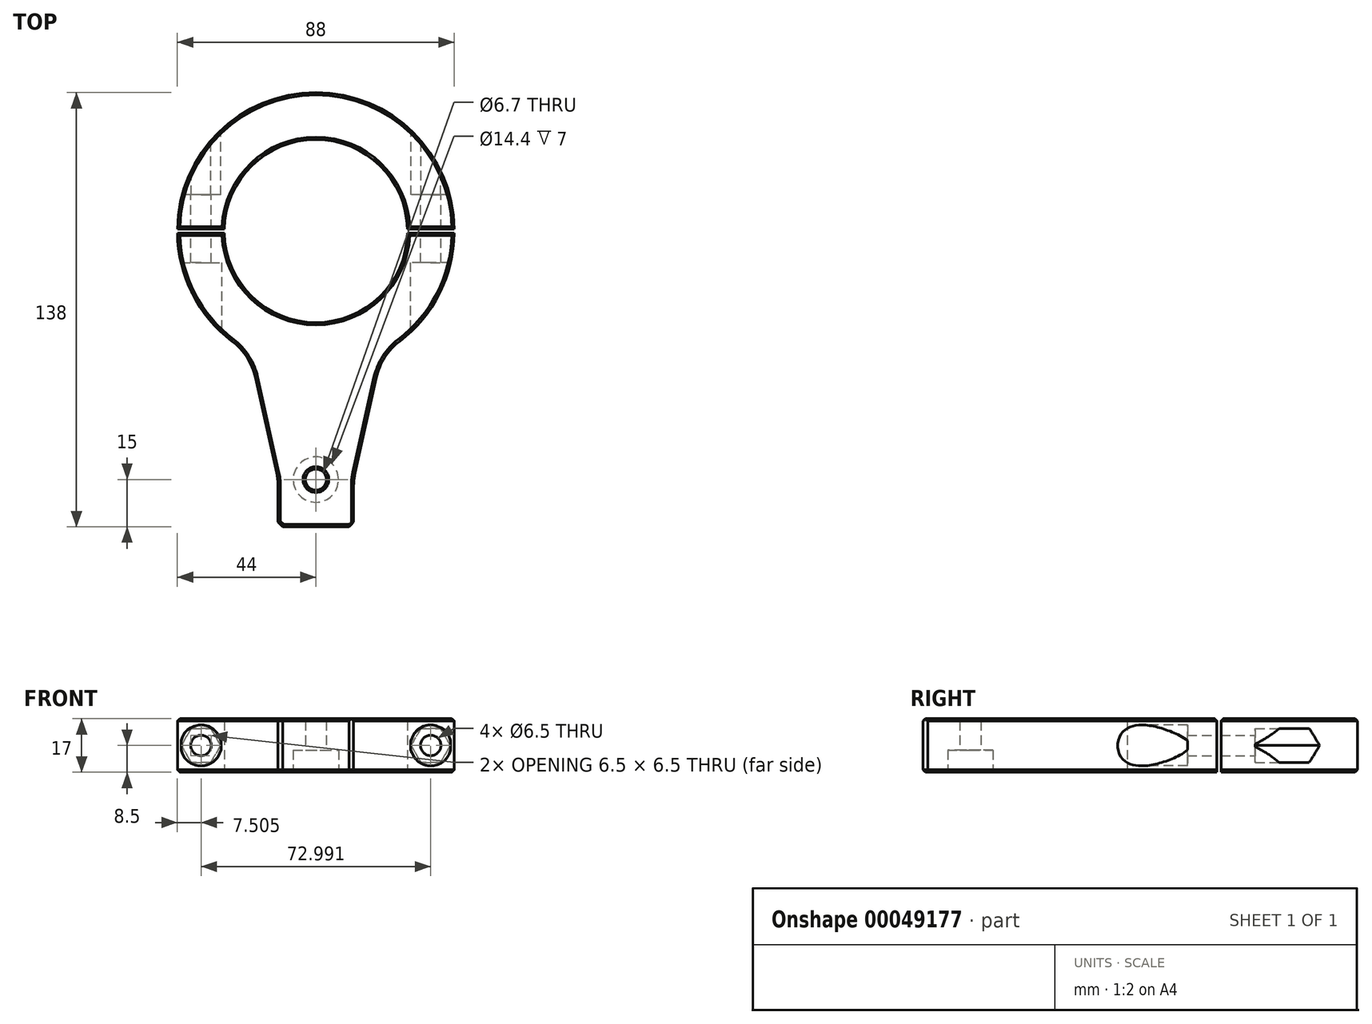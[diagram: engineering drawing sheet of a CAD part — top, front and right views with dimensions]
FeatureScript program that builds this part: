
annotation { "Feature Type Name" : "Feature", "Feature Type Description" : "" }
export const myFeature = defineFeature(function(context is Context, id is Id, definition is map)
    precondition{}
    {
        {
            var Q0;
            Q0=qCreatedBy(makeId("Top.planeOp"),FACE);
            var sketch = newSketch(context, id + "F0", { "sketchPlane" : qUnion([Q0])});
            skArc(sketch, "E0", {"start": v(-29.1, -0.64) * mm, "mid": v(0, -29.1) * mm, "end": v(29.1, -0.64) * mm});
            skArc(sketch, "E1", {"start": v(20.98, -38.68) * mm, "mid": v(37.64, -22.78) * mm, "end": v(44, -0.64) * mm});
            skLineSegment(sketch, "E2.top", {"start": v(-12, -94) * mm, "end": v(12, -94) * mm});
            skLineSegment(sketch, "E2.left", {"start": v(-12, -79) * mm, "end": v(-12, -94) * mm});
            skLineSegment(sketch, "E2.right", {"start": v(12, -79) * mm, "end": v(12, -94) * mm});
            skCircle(sketch, "E3", {"center": v(0, -79) * mm, "radius": 3.35 * mm});
            skPoint(sketch, "E3.centerSnap0", {"position": v(0, -94) * mm});
            skLineSegment(sketch, "E4", {"start": v(-12, -79) * mm, "end": v(-20.98, -38.68) * mm});
            skLineSegment(sketch, "E5", {"start": v(20.98, -38.68) * mm, "end": v(12, -79) * mm});
            skPoint(sketch, "E6.orphan", {"position": v(-12, 0) * mm});
            skLineSegment(sketch, "E7.bottom", {"start": v(-44, 0.64) * mm, "end": v(-29.1, 0.64) * mm});
            skLineSegment(sketch, "E7.top", {"start": v(-44, -0.64) * mm, "end": v(-29.1, -0.64) * mm});
            skLineSegment(sketch, "E8.trimOffspring", {"start": v(29.1, -0.64) * mm, "end": v(44, -0.64) * mm});
            skLineSegment(sketch, "E9.trimOffspring", {"start": v(29.1, 0.64) * mm, "end": v(44, 0.64) * mm});
            skArc(sketch, "E10.trimOffspring", {"start": v(-44, -0.64) * mm, "mid": v(-37.64, -22.78) * mm, "end": v(-20.98, -38.68) * mm});
            skArc(sketch, "E11.trimOffspring", {"start": v(29.1, 0.64) * mm, "mid": v(0, 29.1) * mm, "end": v(-29.1, 0.64) * mm});
            skArc(sketch, "E12.trimOffspring", {"start": v(44, 0.64) * mm, "mid": v(0, 44) * mm, "end": v(-44, 0.64) * mm});
            skSolve(sketch);
        }
        {
            var Q0;
            Q0 = qSketchRegion(id + "F0", true);
            extrude(context, id + "F1", {"entities" : qUnion([Q0]), "depth" : 17 * mm});
        }
        {
            var Q0;
            Q0=makeQuery(id+"F1.opExtrude","CAP_FACE",FACE,{"disambiguationData":[OSD([sQuery(id+"F0.wireOp",EDGE,"E0"),sQuery(id+"F0.wireOp",EDGE,"E1"),sQuery(id+"F0.wireOp",EDGE,"E2.top"),sQuery(id+"F0.wireOp",EDGE,"E2.left"),sQuery(id+"F0.wireOp",EDGE,"E2.right"),sQuery(id+"F0.wireOp",EDGE,"E3"),sQuery(id+"F0.wireOp",EDGE,"E4"),sQuery(id+"F0.wireOp",EDGE,"E5")])],"isStart":true});
            var sketch = newSketch(context, id + "F2", { "sketchPlane" : qUnion([Q0])});
            skCircle(sketch, "E13", {"center": v(0, 79) * mm, "radius": 7.2 * mm});
            skSolve(sketch);
        }
        {
            var Q0;
            Q0 = qSketchRegion(id + "F2", true);
            extrude(context, id + "F3", {"entities" : qUnion([Q0]), "operationType" : NewBodyOperationType.REMOVE, "oppositeDirection" : true, "depth" : 7 * mm});
        }
        {
            var Q0;
            Q0=makeQuery(id+"F1.opExtrude","SWEPT_EDGE",EDGE,{"disambiguationData":[OSD([sQuery(id+"F0.wireOp",EDGE,"E4"),sQuery(id+"F0.wireOp",EDGE,"E10.trimOffspring")])]});
            var Q1;
            Q1=makeQuery(id+"F1.opExtrude","SWEPT_EDGE",EDGE,{"disambiguationData":[OSD([sQuery(id+"F0.wireOp",EDGE,"E2.left"),sQuery(id+"F0.wireOp",EDGE,"E4")])]});
            var Q2;
            Q2=makeQuery(id+"F1.opExtrude","SWEPT_EDGE",EDGE,{"disambiguationData":[OSD([sQuery(id+"F0.wireOp",EDGE,"E1"),sQuery(id+"F0.wireOp",EDGE,"E5")])]});
            var Q3;
            Q3=makeQuery(id+"F1.opExtrude","SWEPT_EDGE",EDGE,{"disambiguationData":[OSD([sQuery(id+"F0.wireOp",EDGE,"E2.right"),sQuery(id+"F0.wireOp",EDGE,"E5")])]});
            fillet(context, id + "F4", {"entities" : qUnion([Q0, Q1, Q2, Q3]), "radius" : 20 * mm, "tangentPropagation" : true, "allowEdgeOverflow" : false});
        }
        {
            var Q0;
            Q0=qCreatedBy(makeId("Front.planeOp"),FACE);
            cPlane(context, id + "F5", {"entities" : qUnion([Q0]), "cplaneType" : CPlaneType.OFFSET, "offset" : 50 * mm, "oppositeDirection" : true, "width" : 150 * mm, "height" : 150 * mm});
        }
        {
            var Q0;
            Q0=qCreatedBy(id+"F5.planeOp",FACE);
            var sketch = newSketch(context, id + "F6", { "sketchPlane" : qUnion([Q0])});
            skCircle(sketch, "E14", {"center": v(36.5, 8.5) * mm, "radius": 3.25 * mm});
            skCircle(sketch, "E15", {"center": v(-36.5, 8.5) * mm, "radius": 3.25 * mm});
            skSolve(sketch);
        }
        {
            var Q0;
            Q0 = qSketchRegion(id + "F6", true);
            extrude(context, id + "F7", {"entities" : qUnion([Q0]), "operationType" : NewBodyOperationType.REMOVE, "depth" : 100 * mm});
        }
        {
            var Q0;
            Q0=qCreatedBy(id+"F5.planeOp",FACE);
            var sketch = newSketch(context, id + "F8", { "sketchPlane" : qUnion([Q0])});
            skCircle(sketch, "E16.cCircle", {"center": v(36.5, 8.5) * mm, "radius": 5.4 * mm, "construction": true});
            skLineSegment(sketch, "E16.0", {"start": v(33.38, 3.1) * mm, "end": v(30.26, 8.5) * mm});
            skLineSegment(sketch, "E16.1", {"start": v(30.26, 8.5) * mm, "end": v(33.38, 13.9) * mm});
            skLineSegment(sketch, "E16.2", {"start": v(33.38, 13.9) * mm, "end": v(39.61, 13.9) * mm});
            skLineSegment(sketch, "E16.3", {"start": v(39.61, 13.9) * mm, "end": v(42.73, 8.5) * mm});
            skLineSegment(sketch, "E16.4", {"start": v(42.73, 8.5) * mm, "end": v(39.61, 3.1) * mm});
            skLineSegment(sketch, "E16.5", {"start": v(39.61, 3.1) * mm, "end": v(33.38, 3.1) * mm});
            skPoint(sketch, "E16.0.midPoint", {"position": v(31.82, 5.8) * mm});
            skCircle(sketch, "E17.cCircle", {"center": v(-36.5, 8.5) * mm, "radius": 5.4 * mm, "construction": true});
            skLineSegment(sketch, "E17.0", {"start": v(-39.61, 3.1) * mm, "end": v(-42.73, 8.5) * mm});
            skLineSegment(sketch, "E17.1", {"start": v(-42.73, 8.5) * mm, "end": v(-39.61, 13.9) * mm});
            skLineSegment(sketch, "E17.2", {"start": v(-39.61, 13.9) * mm, "end": v(-33.38, 13.9) * mm});
            skLineSegment(sketch, "E17.3", {"start": v(-33.38, 13.9) * mm, "end": v(-30.26, 8.5) * mm});
            skLineSegment(sketch, "E17.4", {"start": v(-30.26, 8.5) * mm, "end": v(-33.38, 3.1) * mm});
            skLineSegment(sketch, "E17.5", {"start": v(-33.38, 3.1) * mm, "end": v(-39.61, 3.1) * mm});
            skPoint(sketch, "E17.0.midPoint", {"position": v(-41.17, 5.8) * mm});
            skSolve(sketch);
        }
        {
            var Q0;
            Q0 = qSketchRegion(id + "F8", true);
            extrude(context, id + "F9", {"entities" : qUnion([Q0]), "operationType" : NewBodyOperationType.REMOVE, "depth" : 38.5 * mm});
        }
        {
            var Q0;
            Q0=qCreatedBy(makeId("Front.planeOp"),FACE);
            cPlane(context, id + "F10", {"entities" : qUnion([Q0]), "cplaneType" : CPlaneType.OFFSET, "offset" : 40 * mm, "width" : 150 * mm, "height" : 150 * mm});
        }
        {
            var Q0;
            Q0=qCreatedBy(id+"F10.planeOp",FACE);
            var sketch = newSketch(context, id + "F11", { "sketchPlane" : qUnion([Q0])});
            skCircle(sketch, "E18", {"center": v(-36.5, 8.5) * mm, "radius": 6.5 * mm});
            skCircle(sketch, "E19", {"center": v(36.5, 8.5) * mm, "radius": 6.5 * mm});
            skSolve(sketch);
        }
        {
            var Q0;
            Q0=makeQuery(id+"F11.imprint","IMPRINT",FACE,{"disambiguationData":[TD([[makeQuery(id+"F11.imprint","IMPRINT",EDGE,{"derivedFrom":sQuery(id+"F11.wireOp",EDGE,"E18")}),1.0]])]});
            var Q1;
            Q1=makeQuery(id+"F11.imprint","IMPRINT",FACE,{"disambiguationData":[TD([[makeQuery(id+"F11.imprint","IMPRINT",EDGE,{"derivedFrom":sQuery(id+"F11.wireOp",EDGE,"E19")}),1.0]])]});
            extrude(context, id + "F12", {"entities" : qUnion([Q0, Q1]), "operationType" : NewBodyOperationType.REMOVE, "oppositeDirection" : true, "depth" : 30 * mm});
        }
        {
            var Q0;
            Q0=makeQuery(id+"F1.opExtrude","SWEPT_EDGE",EDGE,{"disambiguationData":[OSD([sQuery(id+"F0.wireOp",EDGE,"E2.top"),sQuery(id+"F0.wireOp",EDGE,"E2.left")])]});
            var Q1;
            Q1=makeQuery(id+"F1.opExtrude","SWEPT_EDGE",EDGE,{"disambiguationData":[OSD([sQuery(id+"F0.wireOp",EDGE,"E2.top"),sQuery(id+"F0.wireOp",EDGE,"E2.right")])]});
            chamfer(context, id + "F13", {"entities" : qUnion([Q0, Q1]), "width" : 1.5 * mm, "tangentPropagation" : true});
        }
        {
            var Q0;
            Q0=makeQuery(id+"F1.opExtrude","CAP_EDGE",EDGE,{"disambiguationData":[OSD([sQuery(id+"F0.wireOp",EDGE,"E3")])],"isStart":false});
            var Q1;
            Q1=makeQuery(id+"F1.opExtrude","CAP_EDGE",EDGE,{"disambiguationData":[OSD([sQuery(id+"F0.wireOp",EDGE,"E0")])],"isStart":false});
            var Q2;
            Q2=makeQuery(id+"F1.opExtrude","CAP_EDGE",EDGE,{"disambiguationData":[OSD([sQuery(id+"F0.wireOp",EDGE,"E11.trimOffspring")])],"isStart":false});
            var Q3;
            Q3=makeQuery(id+"F1.opExtrude","CAP_EDGE",EDGE,{"disambiguationData":[OSD([sQuery(id+"F0.wireOp",EDGE,"E9.trimOffspring")])],"isStart":false});
            var Q4;
            Q4=makeQuery(id+"F1.opExtrude","CAP_EDGE",EDGE,{"disambiguationData":[OSD([sQuery(id+"F0.wireOp",EDGE,"E8.trimOffspring")])],"isStart":false});
            var Q5;
            Q5=makeQuery(id+"F1.opExtrude","CAP_EDGE",EDGE,{"disambiguationData":[OSD([sQuery(id+"F0.wireOp",EDGE,"E7.bottom")])],"isStart":false});
            var Q6;
            Q6=makeQuery(id+"F1.opExtrude","CAP_EDGE",EDGE,{"disambiguationData":[OSD([sQuery(id+"F0.wireOp",EDGE,"E7.top")])],"isStart":false});
            var Q7;
            Q7=makeQuery(id+"F3.boolean.opBoolean","COPY",EDGE,{"derivedFrom":makeQuery(id+"F3.opExtrude","CAP_EDGE",EDGE,{"disambiguationData":[OSD([sQuery(id+"F2.wireOp",EDGE,"E13")])],"isStart":true})});
            var Q8;
            Q8=makeQuery(id+"F1.opExtrude","CAP_EDGE",EDGE,{"disambiguationData":[OSD([sQuery(id+"F0.wireOp",EDGE,"E0")])],"isStart":true});
            var Q9;
            Q9=makeQuery(id+"F1.opExtrude","CAP_EDGE",EDGE,{"disambiguationData":[OSD([sQuery(id+"F0.wireOp",EDGE,"E11.trimOffspring")])],"isStart":true});
            var Q10;
            Q10=makeQuery(id+"F1.opExtrude","CAP_EDGE",EDGE,{"disambiguationData":[OSD([sQuery(id+"F0.wireOp",EDGE,"E1")])],"isStart":true});
            var Q11;
            {var subQ0=sQuery(id+"F0.wireOp",EDGE,"E1");var subQ1=sQuery(id+"F0.wireOp",EDGE,"E5");Q11=makeQuery(id+"F4.opFillet","BLEND_EDGE",EDGE,{"blendedFrom":[makeQuery(id+"F1.opExtrude","SWEPT_EDGE",EDGE,{"disambiguationData":[OSD([subQ0,subQ1])]}),makeQuery(id+"F1.opExtrude","CAP_FACE",FACE,{"disambiguationData":[OSD([sQuery(id+"F0.wireOp",EDGE,"E0"),subQ0,sQuery(id+"F0.wireOp",EDGE,"E2.top"),sQuery(id+"F0.wireOp",EDGE,"E2.left"),sQuery(id+"F0.wireOp",EDGE,"E2.right"),sQuery(id+"F0.wireOp",EDGE,"E3"),sQuery(id+"F0.wireOp",EDGE,"E4"),subQ1,sQuery(id+"F0.wireOp",EDGE,"E7.top"),sQuery(id+"F0.wireOp",EDGE,"E8.trimOffspring"),sQuery(id+"F0.wireOp",EDGE,"E10.trimOffspring")])],"isStart":true})],"blendedInto":[makeQuery(id+"F1.opExtrude","CAP_FACE",FACE,{"disambiguationData":[OSD([sQuery(id+"F0.wireOp",EDGE,"E0"),subQ0,sQuery(id+"F0.wireOp",EDGE,"E2.top"),sQuery(id+"F0.wireOp",EDGE,"E2.left"),sQuery(id+"F0.wireOp",EDGE,"E2.right"),sQuery(id+"F0.wireOp",EDGE,"E3"),sQuery(id+"F0.wireOp",EDGE,"E4"),subQ1,sQuery(id+"F0.wireOp",EDGE,"E7.top"),sQuery(id+"F0.wireOp",EDGE,"E8.trimOffspring"),sQuery(id+"F0.wireOp",EDGE,"E10.trimOffspring")])],"isStart":true})]});}
            var Q12;
            Q12=makeQuery(id+"F1.opExtrude","CAP_EDGE",EDGE,{"disambiguationData":[OSD([sQuery(id+"F0.wireOp",EDGE,"E5")])],"isStart":true});
            var Q13;
            Q13=makeQuery(id+"F1.opExtrude","CAP_EDGE",EDGE,{"disambiguationData":[OSD([sQuery(id+"F0.wireOp",EDGE,"E2.right")])],"isStart":true});
            var Q14;
            {var subQ0=sQuery(id+"F0.wireOp",EDGE,"E2.right");var subQ1=sQuery(id+"F0.wireOp",EDGE,"E5");Q14=makeQuery(id+"F4.opFillet","BLEND_EDGE",EDGE,{"blendedFrom":[makeQuery(id+"F1.opExtrude","SWEPT_EDGE",EDGE,{"disambiguationData":[OSD([subQ0,subQ1])]}),makeQuery(id+"F1.opExtrude","CAP_FACE",FACE,{"disambiguationData":[OSD([sQuery(id+"F0.wireOp",EDGE,"E0"),sQuery(id+"F0.wireOp",EDGE,"E1"),sQuery(id+"F0.wireOp",EDGE,"E2.top"),sQuery(id+"F0.wireOp",EDGE,"E2.left"),subQ0,sQuery(id+"F0.wireOp",EDGE,"E3"),sQuery(id+"F0.wireOp",EDGE,"E4"),subQ1,sQuery(id+"F0.wireOp",EDGE,"E7.top"),sQuery(id+"F0.wireOp",EDGE,"E8.trimOffspring"),sQuery(id+"F0.wireOp",EDGE,"E10.trimOffspring")])],"isStart":true})],"blendedInto":[makeQuery(id+"F1.opExtrude","CAP_FACE",FACE,{"disambiguationData":[OSD([sQuery(id+"F0.wireOp",EDGE,"E0"),sQuery(id+"F0.wireOp",EDGE,"E1"),sQuery(id+"F0.wireOp",EDGE,"E2.top"),sQuery(id+"F0.wireOp",EDGE,"E2.left"),subQ0,sQuery(id+"F0.wireOp",EDGE,"E3"),sQuery(id+"F0.wireOp",EDGE,"E4"),subQ1,sQuery(id+"F0.wireOp",EDGE,"E7.top"),sQuery(id+"F0.wireOp",EDGE,"E8.trimOffspring"),sQuery(id+"F0.wireOp",EDGE,"E10.trimOffspring")])],"isStart":true})]});}
            var Q15;
            {var subQ0=sQuery(id+"F0.wireOp",EDGE,"E2.top");var subQ1=sQuery(id+"F0.wireOp",EDGE,"E2.right");Q15=makeQuery(id+"F13.opChamfer","BLEND_EDGE",EDGE,{"blendedFrom":[makeQuery(id+"F1.opExtrude","SWEPT_EDGE",EDGE,{"disambiguationData":[OSD([subQ0,subQ1])]}),makeQuery(id+"F1.opExtrude","CAP_FACE",FACE,{"disambiguationData":[OSD([sQuery(id+"F0.wireOp",EDGE,"E0"),sQuery(id+"F0.wireOp",EDGE,"E1"),subQ0,sQuery(id+"F0.wireOp",EDGE,"E2.left"),subQ1,sQuery(id+"F0.wireOp",EDGE,"E3"),sQuery(id+"F0.wireOp",EDGE,"E4"),sQuery(id+"F0.wireOp",EDGE,"E5"),sQuery(id+"F0.wireOp",EDGE,"E7.top"),sQuery(id+"F0.wireOp",EDGE,"E8.trimOffspring"),sQuery(id+"F0.wireOp",EDGE,"E10.trimOffspring")])],"isStart":true})],"blendedInto":[makeQuery(id+"F1.opExtrude","CAP_FACE",FACE,{"disambiguationData":[OSD([sQuery(id+"F0.wireOp",EDGE,"E0"),sQuery(id+"F0.wireOp",EDGE,"E1"),subQ0,sQuery(id+"F0.wireOp",EDGE,"E2.left"),subQ1,sQuery(id+"F0.wireOp",EDGE,"E3"),sQuery(id+"F0.wireOp",EDGE,"E4"),sQuery(id+"F0.wireOp",EDGE,"E5"),sQuery(id+"F0.wireOp",EDGE,"E7.top"),sQuery(id+"F0.wireOp",EDGE,"E8.trimOffspring"),sQuery(id+"F0.wireOp",EDGE,"E10.trimOffspring")])],"isStart":true})]});}
            var Q16;
            Q16=makeQuery(id+"F1.opExtrude","CAP_EDGE",EDGE,{"disambiguationData":[OSD([sQuery(id+"F0.wireOp",EDGE,"E2.top")])],"isStart":true});
            var Q17;
            {var subQ0=sQuery(id+"F0.wireOp",EDGE,"E2.top");var subQ1=sQuery(id+"F0.wireOp",EDGE,"E2.left");Q17=makeQuery(id+"F13.opChamfer","BLEND_EDGE",EDGE,{"blendedFrom":[makeQuery(id+"F1.opExtrude","SWEPT_EDGE",EDGE,{"disambiguationData":[OSD([subQ0,subQ1])]}),makeQuery(id+"F1.opExtrude","CAP_FACE",FACE,{"disambiguationData":[OSD([sQuery(id+"F0.wireOp",EDGE,"E0"),sQuery(id+"F0.wireOp",EDGE,"E1"),subQ0,subQ1,sQuery(id+"F0.wireOp",EDGE,"E2.right"),sQuery(id+"F0.wireOp",EDGE,"E3"),sQuery(id+"F0.wireOp",EDGE,"E4"),sQuery(id+"F0.wireOp",EDGE,"E5"),sQuery(id+"F0.wireOp",EDGE,"E7.top"),sQuery(id+"F0.wireOp",EDGE,"E8.trimOffspring"),sQuery(id+"F0.wireOp",EDGE,"E10.trimOffspring")])],"isStart":true})],"blendedInto":[makeQuery(id+"F1.opExtrude","CAP_FACE",FACE,{"disambiguationData":[OSD([sQuery(id+"F0.wireOp",EDGE,"E0"),sQuery(id+"F0.wireOp",EDGE,"E1"),subQ0,subQ1,sQuery(id+"F0.wireOp",EDGE,"E2.right"),sQuery(id+"F0.wireOp",EDGE,"E3"),sQuery(id+"F0.wireOp",EDGE,"E4"),sQuery(id+"F0.wireOp",EDGE,"E5"),sQuery(id+"F0.wireOp",EDGE,"E7.top"),sQuery(id+"F0.wireOp",EDGE,"E8.trimOffspring"),sQuery(id+"F0.wireOp",EDGE,"E10.trimOffspring")])],"isStart":true})]});}
            var Q18;
            Q18=makeQuery(id+"F1.opExtrude","CAP_EDGE",EDGE,{"disambiguationData":[OSD([sQuery(id+"F0.wireOp",EDGE,"E2.left")])],"isStart":true});
            var Q19;
            {var subQ0=sQuery(id+"F0.wireOp",EDGE,"E2.left");var subQ1=sQuery(id+"F0.wireOp",EDGE,"E4");Q19=makeQuery(id+"F4.opFillet","BLEND_EDGE",EDGE,{"blendedFrom":[makeQuery(id+"F1.opExtrude","SWEPT_EDGE",EDGE,{"disambiguationData":[OSD([subQ0,subQ1])]}),makeQuery(id+"F1.opExtrude","CAP_FACE",FACE,{"disambiguationData":[OSD([sQuery(id+"F0.wireOp",EDGE,"E0"),sQuery(id+"F0.wireOp",EDGE,"E1"),sQuery(id+"F0.wireOp",EDGE,"E2.top"),subQ0,sQuery(id+"F0.wireOp",EDGE,"E2.right"),sQuery(id+"F0.wireOp",EDGE,"E3"),subQ1,sQuery(id+"F0.wireOp",EDGE,"E5"),sQuery(id+"F0.wireOp",EDGE,"E7.top"),sQuery(id+"F0.wireOp",EDGE,"E8.trimOffspring"),sQuery(id+"F0.wireOp",EDGE,"E10.trimOffspring")])],"isStart":true})],"blendedInto":[makeQuery(id+"F1.opExtrude","CAP_FACE",FACE,{"disambiguationData":[OSD([sQuery(id+"F0.wireOp",EDGE,"E0"),sQuery(id+"F0.wireOp",EDGE,"E1"),sQuery(id+"F0.wireOp",EDGE,"E2.top"),subQ0,sQuery(id+"F0.wireOp",EDGE,"E2.right"),sQuery(id+"F0.wireOp",EDGE,"E3"),subQ1,sQuery(id+"F0.wireOp",EDGE,"E5"),sQuery(id+"F0.wireOp",EDGE,"E7.top"),sQuery(id+"F0.wireOp",EDGE,"E8.trimOffspring"),sQuery(id+"F0.wireOp",EDGE,"E10.trimOffspring")])],"isStart":true})]});}
            var Q20;
            Q20=makeQuery(id+"F1.opExtrude","CAP_EDGE",EDGE,{"disambiguationData":[OSD([sQuery(id+"F0.wireOp",EDGE,"E4")])],"isStart":true});
            var Q21;
            {var subQ0=sQuery(id+"F0.wireOp",EDGE,"E4");var subQ1=sQuery(id+"F0.wireOp",EDGE,"E10.trimOffspring");Q21=makeQuery(id+"F4.opFillet","BLEND_EDGE",EDGE,{"blendedFrom":[makeQuery(id+"F1.opExtrude","SWEPT_EDGE",EDGE,{"disambiguationData":[OSD([subQ0,subQ1])]}),makeQuery(id+"F1.opExtrude","CAP_FACE",FACE,{"disambiguationData":[OSD([sQuery(id+"F0.wireOp",EDGE,"E0"),sQuery(id+"F0.wireOp",EDGE,"E1"),sQuery(id+"F0.wireOp",EDGE,"E2.top"),sQuery(id+"F0.wireOp",EDGE,"E2.left"),sQuery(id+"F0.wireOp",EDGE,"E2.right"),sQuery(id+"F0.wireOp",EDGE,"E3"),subQ0,sQuery(id+"F0.wireOp",EDGE,"E5"),sQuery(id+"F0.wireOp",EDGE,"E7.top"),sQuery(id+"F0.wireOp",EDGE,"E8.trimOffspring"),subQ1])],"isStart":true})],"blendedInto":[makeQuery(id+"F1.opExtrude","CAP_FACE",FACE,{"disambiguationData":[OSD([sQuery(id+"F0.wireOp",EDGE,"E0"),sQuery(id+"F0.wireOp",EDGE,"E1"),sQuery(id+"F0.wireOp",EDGE,"E2.top"),sQuery(id+"F0.wireOp",EDGE,"E2.left"),sQuery(id+"F0.wireOp",EDGE,"E2.right"),sQuery(id+"F0.wireOp",EDGE,"E3"),subQ0,sQuery(id+"F0.wireOp",EDGE,"E5"),sQuery(id+"F0.wireOp",EDGE,"E7.top"),sQuery(id+"F0.wireOp",EDGE,"E8.trimOffspring"),subQ1])],"isStart":true})]});}
            var Q22;
            Q22=makeQuery(id+"F1.opExtrude","CAP_EDGE",EDGE,{"disambiguationData":[OSD([sQuery(id+"F0.wireOp",EDGE,"E10.trimOffspring")])],"isStart":true});
            var Q23;
            Q23=makeQuery(id+"F1.opExtrude","CAP_EDGE",EDGE,{"disambiguationData":[OSD([sQuery(id+"F0.wireOp",EDGE,"E12.trimOffspring")])],"isStart":true});
            var Q24;
            Q24=makeQuery(id+"F1.opExtrude","CAP_EDGE",EDGE,{"disambiguationData":[OSD([sQuery(id+"F0.wireOp",EDGE,"E5")])],"isStart":false});
            var Q25;
            {var subQ0=sQuery(id+"F0.wireOp",EDGE,"E1");var subQ1=sQuery(id+"F0.wireOp",EDGE,"E5");Q25=makeQuery(id+"F4.opFillet","BLEND_EDGE",EDGE,{"blendedFrom":[makeQuery(id+"F1.opExtrude","SWEPT_EDGE",EDGE,{"disambiguationData":[OSD([subQ0,subQ1])]}),makeQuery(id+"F1.opExtrude","CAP_FACE",FACE,{"disambiguationData":[OSD([sQuery(id+"F0.wireOp",EDGE,"E0"),subQ0,sQuery(id+"F0.wireOp",EDGE,"E2.top"),sQuery(id+"F0.wireOp",EDGE,"E2.left"),sQuery(id+"F0.wireOp",EDGE,"E2.right"),sQuery(id+"F0.wireOp",EDGE,"E3"),sQuery(id+"F0.wireOp",EDGE,"E4"),subQ1,sQuery(id+"F0.wireOp",EDGE,"E7.top"),sQuery(id+"F0.wireOp",EDGE,"E8.trimOffspring"),sQuery(id+"F0.wireOp",EDGE,"E10.trimOffspring")])],"isStart":false})],"blendedInto":[makeQuery(id+"F1.opExtrude","CAP_FACE",FACE,{"disambiguationData":[OSD([sQuery(id+"F0.wireOp",EDGE,"E0"),subQ0,sQuery(id+"F0.wireOp",EDGE,"E2.top"),sQuery(id+"F0.wireOp",EDGE,"E2.left"),sQuery(id+"F0.wireOp",EDGE,"E2.right"),sQuery(id+"F0.wireOp",EDGE,"E3"),sQuery(id+"F0.wireOp",EDGE,"E4"),subQ1,sQuery(id+"F0.wireOp",EDGE,"E7.top"),sQuery(id+"F0.wireOp",EDGE,"E8.trimOffspring"),sQuery(id+"F0.wireOp",EDGE,"E10.trimOffspring")])],"isStart":false})]});}
            var Q26;
            Q26=makeQuery(id+"F1.opExtrude","CAP_EDGE",EDGE,{"disambiguationData":[OSD([sQuery(id+"F0.wireOp",EDGE,"E1")])],"isStart":false});
            var Q27;
            Q27=makeQuery(id+"F1.opExtrude","CAP_EDGE",EDGE,{"disambiguationData":[OSD([sQuery(id+"F0.wireOp",EDGE,"E4")])],"isStart":false});
            var Q28;
            Q28=makeQuery(id+"F1.opExtrude","CAP_EDGE",EDGE,{"disambiguationData":[OSD([sQuery(id+"F0.wireOp",EDGE,"E2.left")])],"isStart":false});
            var Q29;
            {var subQ0=sQuery(id+"F0.wireOp",EDGE,"E2.left");var subQ1=sQuery(id+"F0.wireOp",EDGE,"E4");Q29=makeQuery(id+"F4.opFillet","BLEND_EDGE",EDGE,{"blendedFrom":[makeQuery(id+"F1.opExtrude","SWEPT_EDGE",EDGE,{"disambiguationData":[OSD([subQ0,subQ1])]}),makeQuery(id+"F1.opExtrude","CAP_FACE",FACE,{"disambiguationData":[OSD([sQuery(id+"F0.wireOp",EDGE,"E0"),sQuery(id+"F0.wireOp",EDGE,"E1"),sQuery(id+"F0.wireOp",EDGE,"E2.top"),subQ0,sQuery(id+"F0.wireOp",EDGE,"E2.right"),sQuery(id+"F0.wireOp",EDGE,"E3"),subQ1,sQuery(id+"F0.wireOp",EDGE,"E5"),sQuery(id+"F0.wireOp",EDGE,"E7.top"),sQuery(id+"F0.wireOp",EDGE,"E8.trimOffspring"),sQuery(id+"F0.wireOp",EDGE,"E10.trimOffspring")])],"isStart":false})],"blendedInto":[makeQuery(id+"F1.opExtrude","CAP_FACE",FACE,{"disambiguationData":[OSD([sQuery(id+"F0.wireOp",EDGE,"E0"),sQuery(id+"F0.wireOp",EDGE,"E1"),sQuery(id+"F0.wireOp",EDGE,"E2.top"),subQ0,sQuery(id+"F0.wireOp",EDGE,"E2.right"),sQuery(id+"F0.wireOp",EDGE,"E3"),subQ1,sQuery(id+"F0.wireOp",EDGE,"E5"),sQuery(id+"F0.wireOp",EDGE,"E7.top"),sQuery(id+"F0.wireOp",EDGE,"E8.trimOffspring"),sQuery(id+"F0.wireOp",EDGE,"E10.trimOffspring")])],"isStart":false})]});}
            var Q30;
            {var subQ0=sQuery(id+"F0.wireOp",EDGE,"E2.top");var subQ1=sQuery(id+"F0.wireOp",EDGE,"E2.left");Q30=makeQuery(id+"F13.opChamfer","BLEND_EDGE",EDGE,{"blendedFrom":[makeQuery(id+"F1.opExtrude","SWEPT_EDGE",EDGE,{"disambiguationData":[OSD([subQ0,subQ1])]}),makeQuery(id+"F1.opExtrude","CAP_FACE",FACE,{"disambiguationData":[OSD([sQuery(id+"F0.wireOp",EDGE,"E0"),sQuery(id+"F0.wireOp",EDGE,"E1"),subQ0,subQ1,sQuery(id+"F0.wireOp",EDGE,"E2.right"),sQuery(id+"F0.wireOp",EDGE,"E3"),sQuery(id+"F0.wireOp",EDGE,"E4"),sQuery(id+"F0.wireOp",EDGE,"E5"),sQuery(id+"F0.wireOp",EDGE,"E7.top"),sQuery(id+"F0.wireOp",EDGE,"E8.trimOffspring"),sQuery(id+"F0.wireOp",EDGE,"E10.trimOffspring")])],"isStart":false})],"blendedInto":[makeQuery(id+"F1.opExtrude","CAP_FACE",FACE,{"disambiguationData":[OSD([sQuery(id+"F0.wireOp",EDGE,"E0"),sQuery(id+"F0.wireOp",EDGE,"E1"),subQ0,subQ1,sQuery(id+"F0.wireOp",EDGE,"E2.right"),sQuery(id+"F0.wireOp",EDGE,"E3"),sQuery(id+"F0.wireOp",EDGE,"E4"),sQuery(id+"F0.wireOp",EDGE,"E5"),sQuery(id+"F0.wireOp",EDGE,"E7.top"),sQuery(id+"F0.wireOp",EDGE,"E8.trimOffspring"),sQuery(id+"F0.wireOp",EDGE,"E10.trimOffspring")])],"isStart":false})]});}
            var Q31;
            Q31=makeQuery(id+"F1.opExtrude","CAP_EDGE",EDGE,{"disambiguationData":[OSD([sQuery(id+"F0.wireOp",EDGE,"E2.top")])],"isStart":false});
            var Q32;
            Q32=makeQuery(id+"F1.opExtrude","CAP_EDGE",EDGE,{"disambiguationData":[OSD([sQuery(id+"F0.wireOp",EDGE,"E2.right")])],"isStart":false});
            var Q33;
            Q33=makeQuery(id+"F1.opExtrude","CAP_EDGE",EDGE,{"disambiguationData":[OSD([sQuery(id+"F0.wireOp",EDGE,"E12.trimOffspring")])],"isStart":false});
            var Q34;
            Q34=makeQuery(id+"F1.opExtrude","CAP_EDGE",EDGE,{"disambiguationData":[OSD([sQuery(id+"F0.wireOp",EDGE,"E10.trimOffspring")])],"isStart":false});
            var Q35;
            {var subQ0=sQuery(id+"F0.wireOp",EDGE,"E4");var subQ1=sQuery(id+"F0.wireOp",EDGE,"E10.trimOffspring");Q35=makeQuery(id+"F4.opFillet","BLEND_EDGE",EDGE,{"blendedFrom":[makeQuery(id+"F1.opExtrude","SWEPT_EDGE",EDGE,{"disambiguationData":[OSD([subQ0,subQ1])]}),makeQuery(id+"F1.opExtrude","CAP_FACE",FACE,{"disambiguationData":[OSD([sQuery(id+"F0.wireOp",EDGE,"E0"),sQuery(id+"F0.wireOp",EDGE,"E1"),sQuery(id+"F0.wireOp",EDGE,"E2.top"),sQuery(id+"F0.wireOp",EDGE,"E2.left"),sQuery(id+"F0.wireOp",EDGE,"E2.right"),sQuery(id+"F0.wireOp",EDGE,"E3"),subQ0,sQuery(id+"F0.wireOp",EDGE,"E5"),sQuery(id+"F0.wireOp",EDGE,"E7.top"),sQuery(id+"F0.wireOp",EDGE,"E8.trimOffspring"),subQ1])],"isStart":false})],"blendedInto":[makeQuery(id+"F1.opExtrude","CAP_FACE",FACE,{"disambiguationData":[OSD([sQuery(id+"F0.wireOp",EDGE,"E0"),sQuery(id+"F0.wireOp",EDGE,"E1"),sQuery(id+"F0.wireOp",EDGE,"E2.top"),sQuery(id+"F0.wireOp",EDGE,"E2.left"),sQuery(id+"F0.wireOp",EDGE,"E2.right"),sQuery(id+"F0.wireOp",EDGE,"E3"),subQ0,sQuery(id+"F0.wireOp",EDGE,"E5"),sQuery(id+"F0.wireOp",EDGE,"E7.top"),sQuery(id+"F0.wireOp",EDGE,"E8.trimOffspring"),subQ1])],"isStart":false})]});}
            chamfer(context, id + "F14", {"entities" : qUnion([Q0, Q1, Q2, Q3, Q4, Q5, Q6, Q7, Q8, Q9, Q10, Q11, Q12, Q13, Q14, Q15, Q16, Q17, Q18, Q19, Q20, Q21, Q22, Q23, Q24, Q25, Q26, Q27, Q28, Q29, Q30, Q31, Q32, Q33, Q34, Q35]), "width" : .75 * mm, "tangentPropagation" : true});
        }
    });
